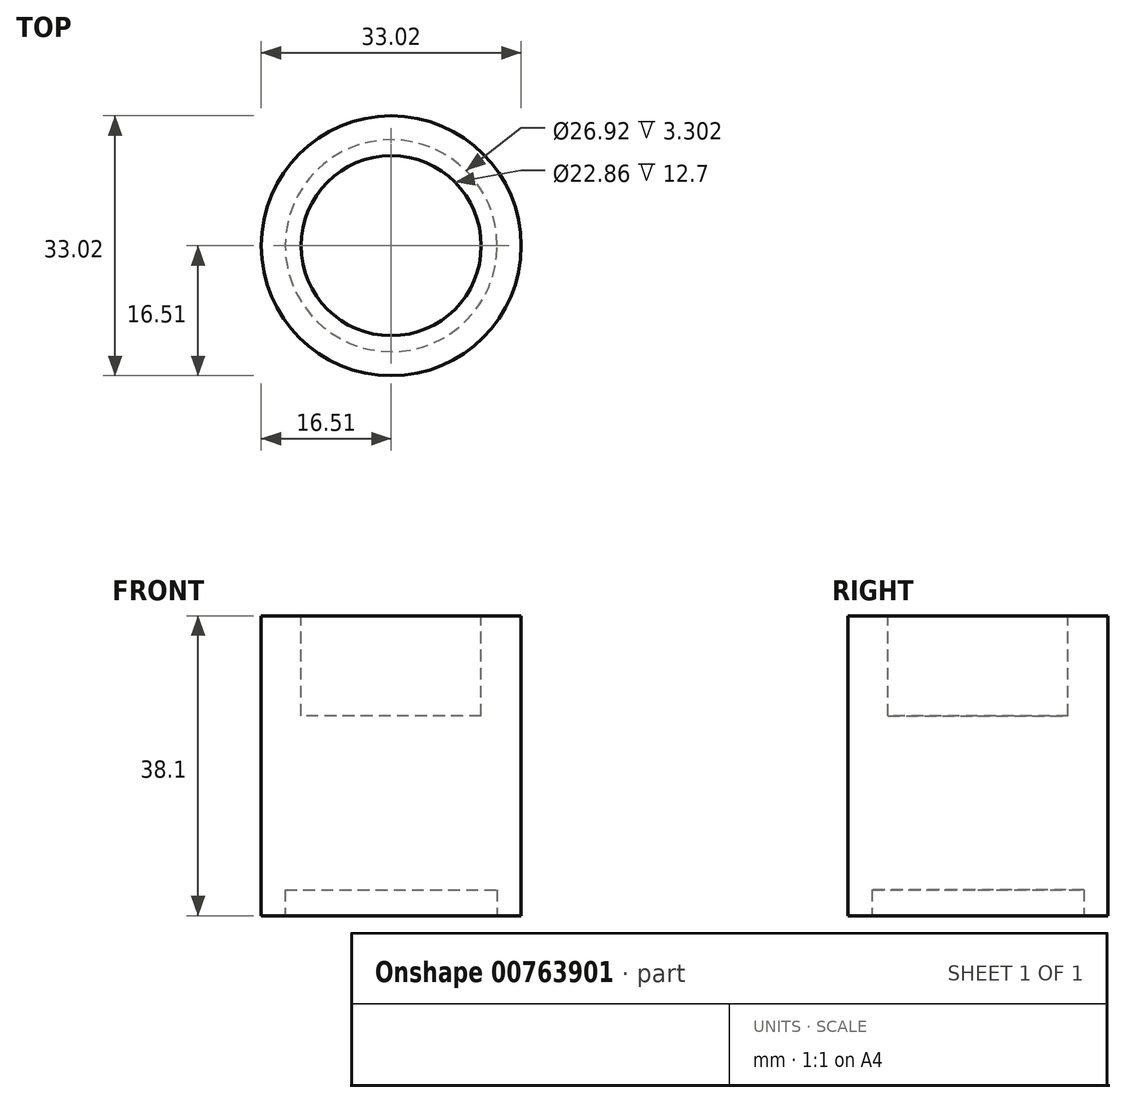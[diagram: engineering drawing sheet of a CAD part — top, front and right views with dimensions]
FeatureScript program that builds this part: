
annotation { "Feature Type Name" : "Feature", "Feature Type Description" : "" }
export const myFeature = defineFeature(function(context is Context, id is Id, definition is map)
    precondition{}
    {
        {
            var Q0;
            Q0=qCreatedBy(makeId("Top.planeOp"),FACE);
            var sketch = newSketch(context, id + "F0", { "sketchPlane" : qUnion([Q0])});
            skCircle(sketch, "E0", {"center": v(0, 0) * mm, "radius": 16.51 * mm});
            skSolve(sketch);
        }
        {
            var Q0;
            Q0 = qSketchRegion(id + "F0", true);
            extrude(context, id + "F1", {"entities" : qUnion([Q0]), "depth" : 38.1 * mm, "offsetDistance" : 25.4 * mm});
        }
        {
            var Q0;
            Q0=makeQuery(id+"F1.opExtrude","CAP_FACE",FACE,{"disambiguationData":[OSD([sQuery(id+"F0.wireOp",EDGE,"E0")])],"isStart":true});
            var sketch = newSketch(context, id + "F2", { "sketchPlane" : qUnion([Q0])});
            skCircle(sketch, "E1", {"center": v(0, 0) * mm, "radius": 13.46 * mm});
            skSolve(sketch);
        }
        {
            var Q0;
            Q0=makeQuery(id+"F2.imprint","IMPRINT",FACE,{"disambiguationData":[TD([[makeQuery(id+"F2.imprint","IMPRINT",EDGE,{"derivedFrom":sQuery(id+"F2.wireOp",EDGE,"E1")}),1.0]])]});
            extrude(context, id + "F3", {"entities" : qUnion([Q0]), "operationType" : NewBodyOperationType.REMOVE, "oppositeDirection" : true, "depth" : 3.3 * mm, "offsetDistance" : 25.4 * mm});
        }
        {
            var Q0;
            Q0=makeQuery(id+"F1.opExtrude","CAP_FACE",FACE,{"disambiguationData":[OSD([sQuery(id+"F0.wireOp",EDGE,"E0")])],"isStart":false});
            var sketch = newSketch(context, id + "F4", { "sketchPlane" : qUnion([Q0])});
            skCircle(sketch, "E2", {"center": v(0, 0) * mm, "radius": 11.43 * mm});
            skSolve(sketch);
        }
        {
            var Q0;
            Q0 = qSketchRegion(id + "F4", true);
            extrude(context, id + "F5", {"entities" : qUnion([Q0]), "operationType" : NewBodyOperationType.REMOVE, "oppositeDirection" : true, "depth" : 12.7 * mm, "offsetDistance" : 25.4 * mm});
        }
    });
